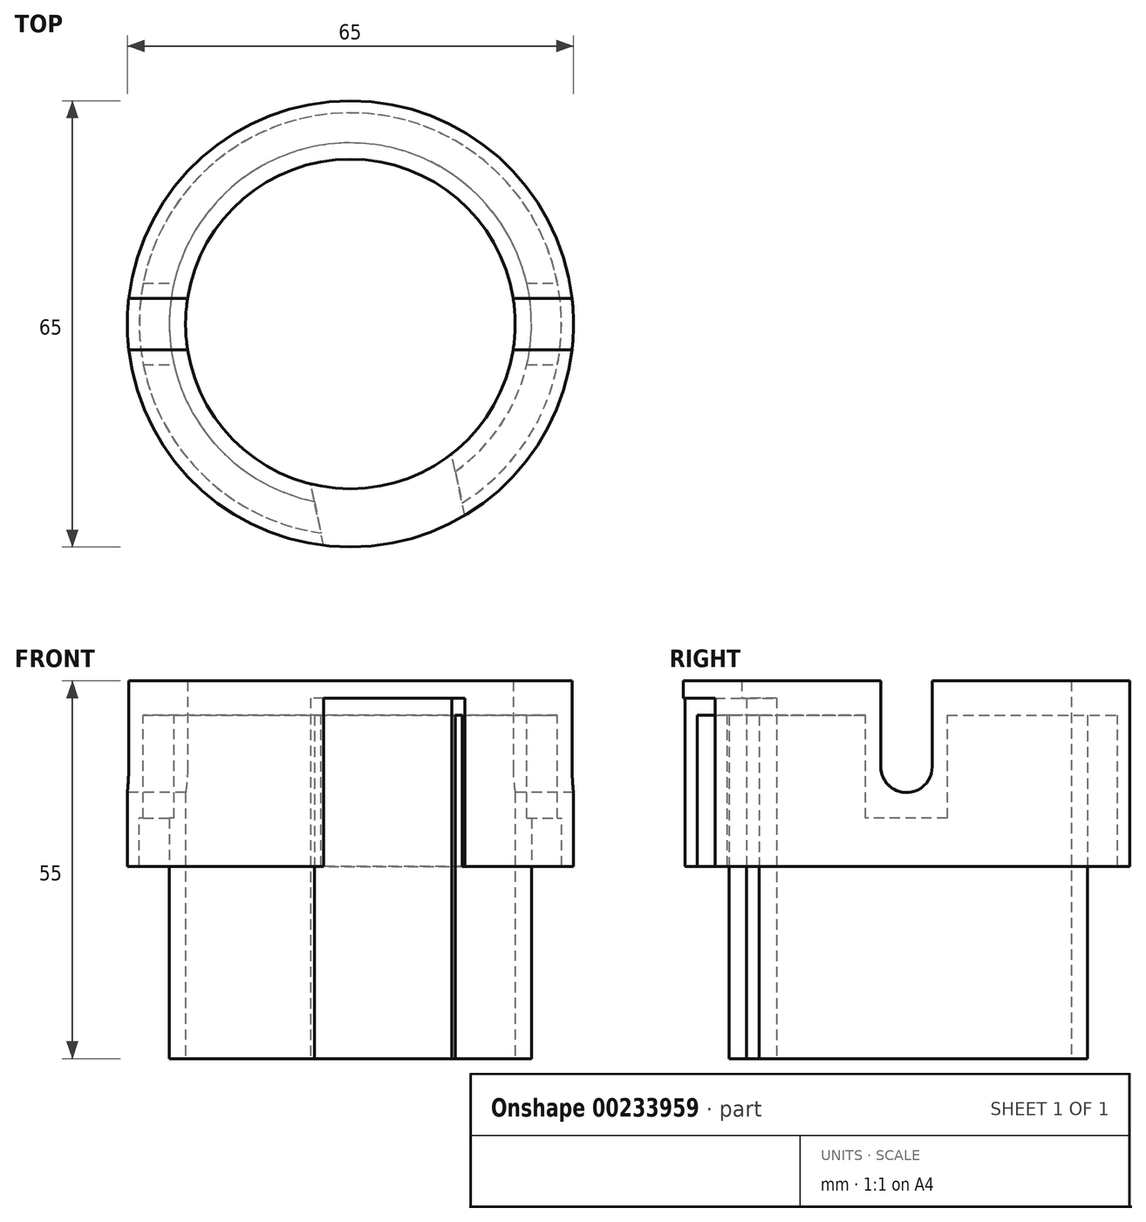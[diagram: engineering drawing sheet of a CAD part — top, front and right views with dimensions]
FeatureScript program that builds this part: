
annotation { "Feature Type Name" : "Feature", "Feature Type Description" : "" }
export const myFeature = defineFeature(function(context is Context, id is Id, definition is map)
    precondition{}
    {
        {
            var Q0;
            Q0=qCreatedBy(makeId("Top.planeOp"),FACE);
            var sketch = newSketch(context, id + "F0", { "sketchPlane" : qUnion([Q0])});
            skCircle(sketch, "E0", {"center": v(0, 0) * mm, "radius": 24 * mm});
            skCircle(sketch, "E1", {"center": v(0, 0) * mm, "radius": 26.38 * mm});
            skSolve(sketch);
        }
        {
            var Q0;
            Q0 = qSketchRegion(id + "F0", true);
            extrude(context, id + "F1", {"entities" : qUnion([Q0]), "depth" : 55 * mm});
        }
        {
            var Q0;
            Q0=makeQuery(id+"F1.opExtrude","CAP_FACE",FACE,{"disambiguationData":[OSD([sQuery(id+"F0.wireOp",EDGE,"E0"),sQuery(id+"F0.wireOp",EDGE,"E1")])],"isStart":false});
            var sketch = newSketch(context, id + "F2", { "sketchPlane" : qUnion([Q0])});
            skCircle(sketch, "E2.0", {"center": v(0, 0) * mm, "radius": 26.38 * mm});
            skCircle(sketch, "E3", {"center": v(0, 0) * mm, "radius": 32.5 * mm});
            skSolve(sketch);
        }
        {
            var Q0;
            Q0 = qSketchRegion(id + "F2", true);
            extrude(context, id + "F3", {"entities" : qUnion([Q0]), "operationType" : NewBodyOperationType.ADD, "oppositeDirection" : true, "depth" : 5 * mm});
        }
        {
            var Q0;
            Q0=makeQuery(id+"F3.opExtrude","CAP_FACE",FACE,{"disambiguationData":[OSD([sQuery(id+"F2.wireOp",EDGE,"E2.0"),sQuery(id+"F2.wireOp",EDGE,"E3")])],"isStart":false});
            var sketch = newSketch(context, id + "F4", { "sketchPlane" : qUnion([Q0])});
            skCircle(sketch, "E4.0", {"center": v(0, 0) * mm, "radius": 32.5 * mm});
            skCircle(sketch, "E5", {"center": v(0, 0) * mm, "radius": 30.75 * mm});
            skSolve(sketch);
        }
        {
            var Q0;
            Q0 = qSketchRegion(id + "F4", true);
            extrude(context, id + "F5", {"entities" : qUnion([Q0]), "operationType" : NewBodyOperationType.ADD, "depth" : 22 * mm});
        }
        {
            var Q0;
            Q0=makeQuery(id+"F3.opExtrude","CAP_FACE",FACE,{"disambiguationData":[OSD([sQuery(id+"F2.wireOp",EDGE,"E2.0"),sQuery(id+"F2.wireOp",EDGE,"E3")])],"isStart":false});
            var sketch = newSketch(context, id + "F6", { "sketchPlane" : qUnion([Q0])});
            skLineSegment(sketch, "E6", {"start": v(0, 0) * mm, "end": v(-30.75, 0) * mm, "construction": true});
            skArc(sketch, "E7.0", {"start": v(-25.7, 5.95) * mm, "mid": v(-26.38, 0) * mm, "end": v(-25.7, -5.95) * mm});
            skArc(sketch, "E8.0", {"start": v(-30.17, 5.95) * mm, "mid": v(-30.75, 0) * mm, "end": v(-30.17, -5.95) * mm});
            skLineSegment(sketch, "E9", {"start": v(-30.17, 5.95) * mm, "end": v(-25.7, 5.95) * mm});
            skLineSegment(sketch, "E10", {"start": v(-30.17, -5.95) * mm, "end": v(-25.7, -5.95) * mm});
            skLineSegment(sketch, "E11", {"start": v(25.7, 5.95) * mm, "end": v(30.17, 5.95) * mm});
            skLineSegment(sketch, "E12", {"start": v(25.7, -5.95) * mm, "end": v(30.17, -5.95) * mm});
            skArc(sketch, "E13.trimOffspring", {"start": v(30.17, -5.95) * mm, "mid": v(30.75, 0) * mm, "end": v(30.17, 5.95) * mm});
            skArc(sketch, "E14.trimOffspring", {"start": v(25.7, -5.95) * mm, "mid": v(26.38, 0) * mm, "end": v(25.7, 5.95) * mm});
            skSolve(sketch);
        }
        {
            var Q0;
            Q0 = qSketchRegion(id + "F6", true);
            extrude(context, id + "F7", {"entities" : qUnion([Q0]), "operationType" : NewBodyOperationType.ADD, "depth" : 15 * mm});
        }
        {
            var Q0;
            Q0=qCreatedBy(makeId("Right.planeOp"),FACE);
            var sketch = newSketch(context, id + "F8", { "sketchPlane" : qUnion([Q0])});
            skLineSegment(sketch, "E15", {"start": v(-3.75, 55) * mm, "end": v(3.75, 55) * mm});
            skLineSegment(sketch, "E16", {"start": v(3.75, 55) * mm, "end": v(3.75, 42.5) * mm});
            skLineSegment(sketch, "E17", {"start": v(-3.75, 55) * mm, "end": v(-3.75, 42.5) * mm});
            skLineSegment(sketch, "E18", {"start": v(0, 0) * mm, "end": v(0, 55) * mm, "construction": true});
            skArc(sketch, "E19", {"start": v(-3.75, 42.5) * mm, "mid": v(0, 38.75) * mm, "end": v(3.75, 42.5) * mm});
            skSolve(sketch);
        }
        {
            var Q0;
            Q0 = qSketchRegion(id + "F8", true);
            extrude(context, id + "F9", {"entities" : qUnion([Q0]), "operationType" : NewBodyOperationType.REMOVE, "endBound" : BoundingType.THROUGH_ALL, "depth" : 25 * mm, "hasSecondDirection" : true, "secondDirectionBound" : BoundingType.THROUGH_ALL, "secondDirectionOppositeDirection" : true, "secondDirectionDepth" : 25 * mm});
        }
        {
            var Q0;
            Q0=qCreatedBy(makeId("Front.planeOp"),FACE);
            var Q1;
            Q1=sQuery(id+"F8.wireOp",EDGE,"E18");
            cPlane(context, id + "F10", {"entities" : qUnion([Q0, Q1]), "cplaneType" : CPlaneType.LINE_ANGLE, "offset" : 25 * mm, "angle" : 12 * degree, "width" : 150 * mm, "height" : 150 * mm});
        }
        {
            var Q0;
            Q0=qCreatedBy(id+"F10.planeOp",FACE);
            var sketch = newSketch(context, id + "F11", { "sketchPlane" : qUnion([Q0])});
            skLineSegment(sketch, "E20.bottom", {"start": v(-10.5, 0) * mm, "end": v(10.5, 0) * mm});
            skLineSegment(sketch, "E20.top", {"start": v(-10.5, 52.5) * mm, "end": v(10.5, 52.5) * mm});
            skLineSegment(sketch, "E20.left", {"start": v(-10.5, 0) * mm, "end": v(-10.5, 52.5) * mm});
            skLineSegment(sketch, "E20.right", {"start": v(10.5, 0) * mm, "end": v(10.5, 52.5) * mm});
            skSolve(sketch);
        }
        {
            var Q0;
            Q0 = qSketchRegion(id + "F11", true);
            extrude(context, id + "F12", {"entities" : qUnion([Q0]), "operationType" : NewBodyOperationType.REMOVE, "endBound" : BoundingType.THROUGH_ALL, "oppositeDirection" : true, "depth" : 25 * mm});
        }
    });
